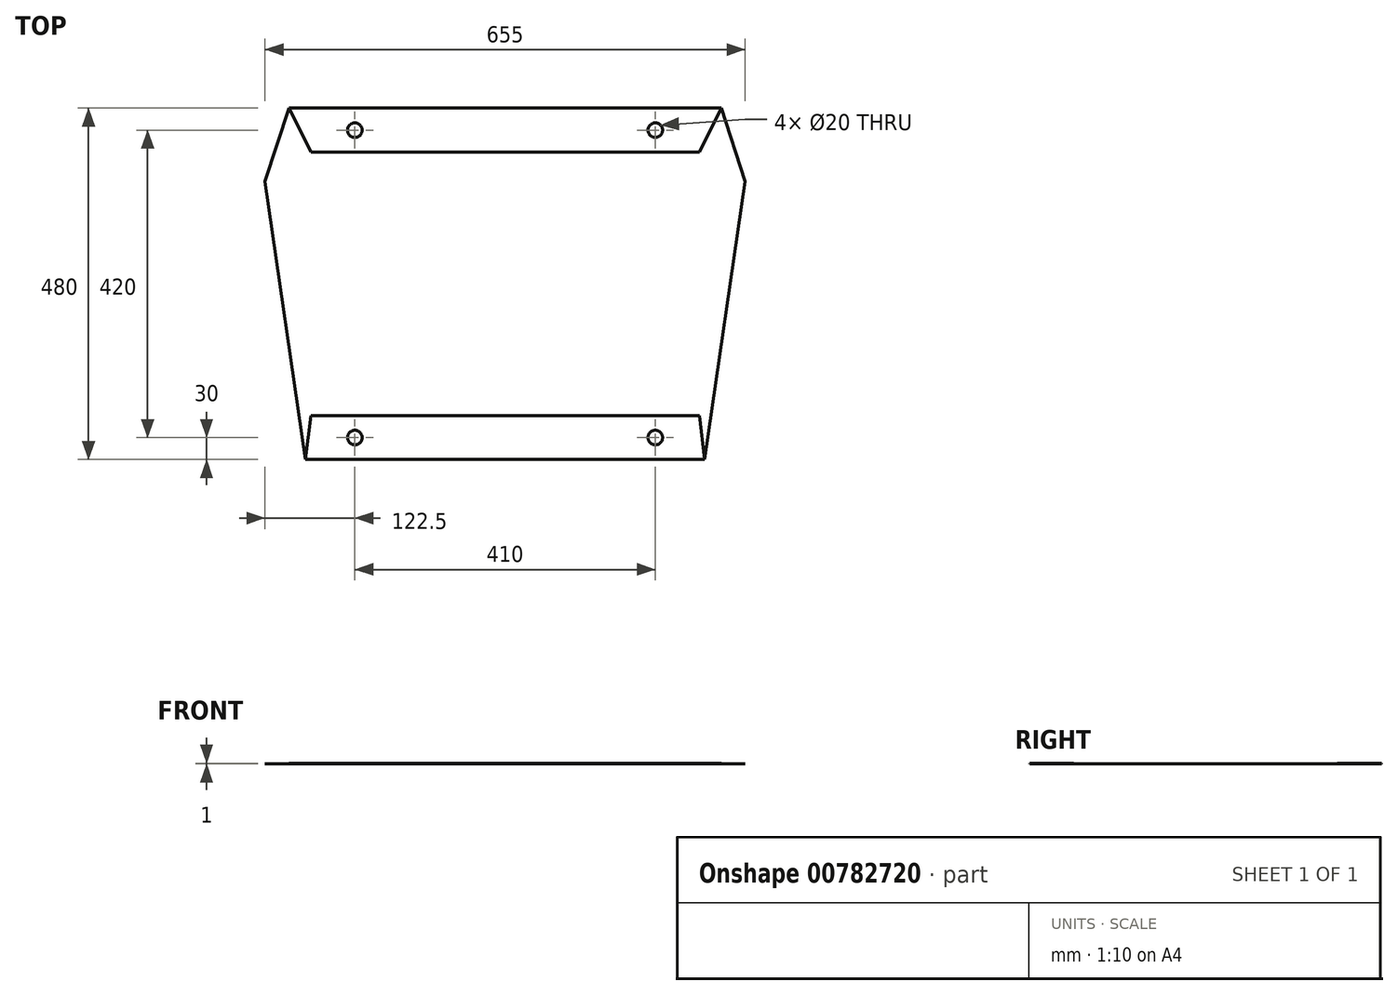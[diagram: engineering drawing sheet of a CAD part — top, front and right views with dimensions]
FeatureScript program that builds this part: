
annotation { "Feature Type Name" : "Feature", "Feature Type Description" : "" }
export const myFeature = defineFeature(function(context is Context, id is Id, definition is map)
    precondition{}
    {
        {
            var Q0;
            Q0=qCreatedBy(makeId("Top.planeOp"),FACE);
            var sketch = newSketch(context, id + "F0", { "sketchPlane" : qUnion([Q0])});
            skLineSegment(sketch, "E0", {"start": v(-590, 0) * mm, "end": v(0, 0) * mm});
            skLineSegment(sketch, "E1", {"start": v(0, 0) * mm, "end": v(32.5, -100) * mm});
            skLineSegment(sketch, "E2", {"start": v(32.5, -100) * mm, "end": v(-22.5, -480) * mm});
            skLineSegment(sketch, "E3", {"start": v(-22.5, -480) * mm, "end": v(-567.5, -480) * mm});
            skLineSegment(sketch, "E4", {"start": v(-567.5, -480) * mm, "end": v(-622.5, -100) * mm});
            skLineSegment(sketch, "E5", {"start": v(-622.5, -100) * mm, "end": v(-590, 0) * mm});
            skSolve(sketch);
        }
        {
            var Q0;
            Q0 = qSketchRegion(id + "F0", true);
            extrude(context, id + "F1", {"entities" : qUnion([Q0]), "depth" : .5 * mm, "offsetDistance" : 25 * mm});
        }
        {
            var Q0;
            Q0=makeQuery(id+"F1.opExtrude","CAP_FACE",FACE,{"disambiguationData":[OSD([sQuery(id+"F0.wireOp",EDGE,"E0"),sQuery(id+"F0.wireOp",EDGE,"E1"),sQuery(id+"F0.wireOp",EDGE,"E2"),sQuery(id+"F0.wireOp",EDGE,"E3"),sQuery(id+"F0.wireOp",EDGE,"E4"),sQuery(id+"F0.wireOp",EDGE,"E5")])],"isStart":false});
            var sketch = newSketch(context, id + "F2", { "sketchPlane" : qUnion([Q0])});
            skLineSegment(sketch, "E6", {"start": v(-590, 0) * mm, "end": v(-560, -60) * mm});
            skLineSegment(sketch, "E7", {"start": v(-560, -60) * mm, "end": v(-30, -60) * mm});
            skLineSegment(sketch, "E8", {"start": v(-30, -60) * mm, "end": v(0, 0) * mm});
            skLineSegment(sketch, "E9", {"start": v(0, 0) * mm, "end": v(-590, 0) * mm});
            skLineSegment(sketch, "E10.0", {"start": v(-22.5, -480) * mm, "end": v(-567.5, -480) * mm});
            skLineSegment(sketch, "E11", {"start": v(-567.5, -480) * mm, "end": v(-560, -420) * mm});
            skLineSegment(sketch, "E12", {"start": v(-560, -420) * mm, "end": v(-30, -420) * mm});
            skLineSegment(sketch, "E13", {"start": v(-30, -420) * mm, "end": v(-22.5, -480) * mm});
            skSolve(sketch);
        }
        {
            var Q0;
            Q0 = qSketchRegion(id + "F2", true);
            extrude(context, id + "F3", {"entities" : qUnion([Q0]), "operationType" : NewBodyOperationType.ADD, "depth" : .5 * mm, "offsetDistance" : 25 * mm});
        }
        {
            var Q0;
            Q0=makeQuery(id+"F3.opExtrude","CAP_FACE",FACE,{"disambiguationData":[OSD([sQuery(id+"F2.wireOp",EDGE,"E6"),sQuery(id+"F2.wireOp",EDGE,"E7"),sQuery(id+"F2.wireOp",EDGE,"E8"),sQuery(id+"F2.wireOp",EDGE,"E9")])],"isStart":false});
            var sketch = newSketch(context, id + "F4", { "sketchPlane" : qUnion([Q0])});
            skCircle(sketch, "E14", {"center": v(-500, -30) * mm, "radius": 10 * mm});
            skCircle(sketch, "E15.0.1.0", {"center": v(-500, -450) * mm, "radius": 10 * mm});
            skCircle(sketch, "E15.1.0.0", {"center": v(-90, -30) * mm, "radius": 10 * mm});
            skCircle(sketch, "E15.1.1.0", {"center": v(-90, -450) * mm, "radius": 10 * mm});
            skLineSegment(sketch, "E15.direction1", {"start": v(-500, -30) * mm, "end": v(-90, -30) * mm, "construction": true});
            skLineSegment(sketch, "E15.direction2", {"start": v(-500, -30) * mm, "end": v(-500, -450) * mm, "construction": true});
            skSolve(sketch);
        }
        {
            var Q0;
            Q0 = qSketchRegion(id + "F4", true);
            extrude(context, id + "F5", {"entities" : qUnion([Q0]), "operationType" : NewBodyOperationType.REMOVE, "endBound" : BoundingType.THROUGH_ALL, "oppositeDirection" : true, "depth" : 25 * mm, "offsetDistance" : 25 * mm});
        }
    });
